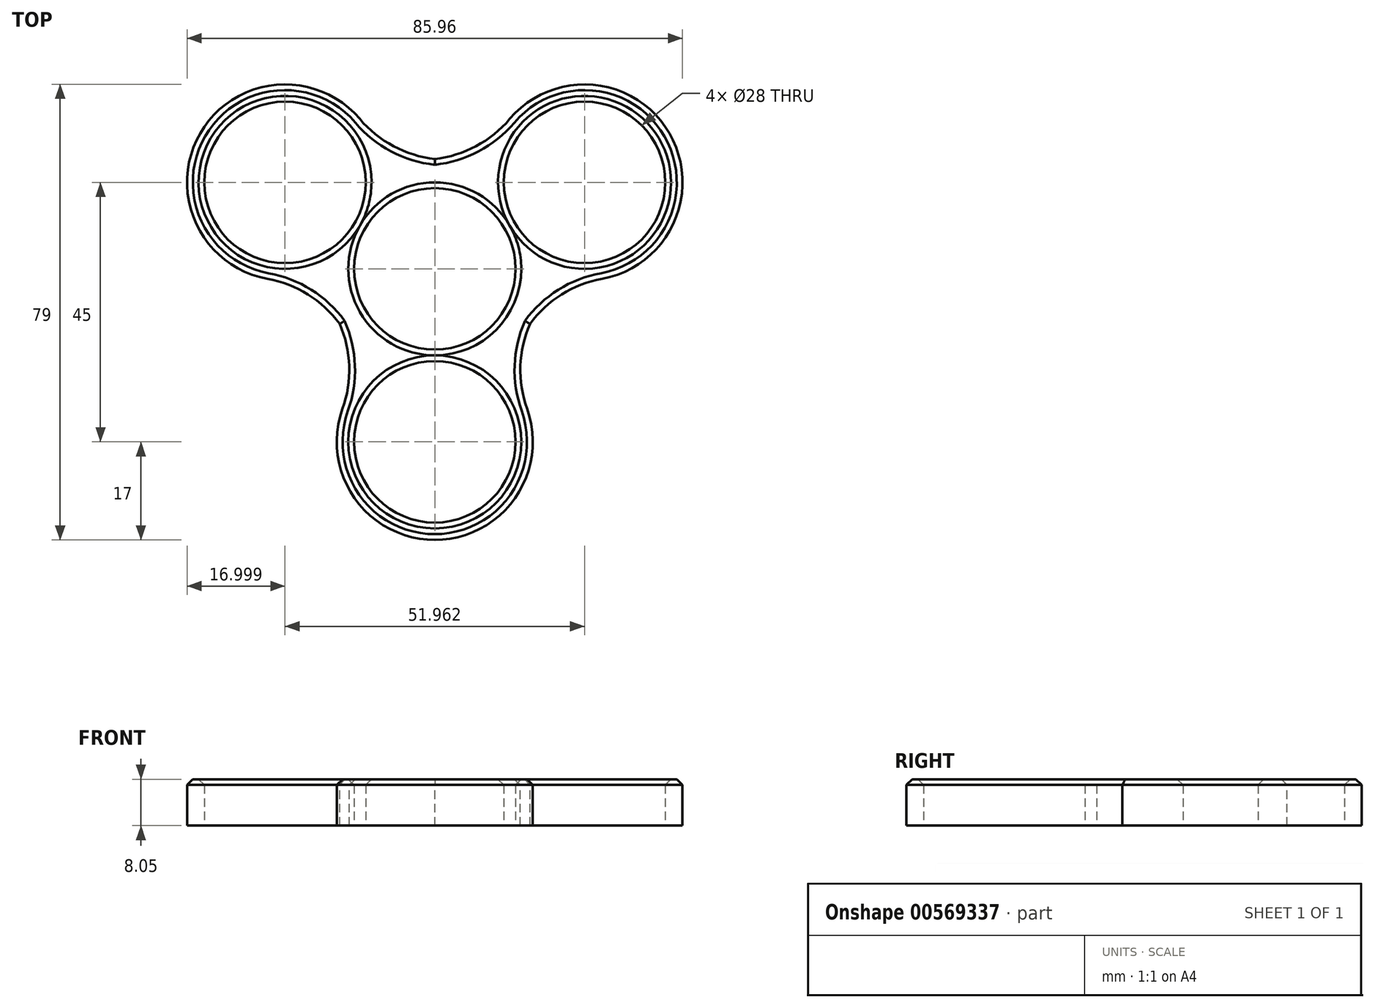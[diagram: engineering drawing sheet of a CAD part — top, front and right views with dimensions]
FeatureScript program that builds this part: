
annotation { "Feature Type Name" : "Feature", "Feature Type Description" : "" }
export const myFeature = defineFeature(function(context is Context, id is Id, definition is map)
    precondition{}
    {
        {
            var Q0;
            Q0=qCreatedBy(makeId("Top.planeOp"),FACE);
            var sketch = newSketch(context, id + "F0", { "sketchPlane" : qUnion([Q0])});
            skCircle(sketch, "E0", {"center": v(0, 0) * mm, "radius": 5.9 * mm});
            skCircle(sketch, "E1", {"center": v(0, 0) * mm, "radius": 14 * mm});
            skArc(sketch, "E2", {"start": v(5.9, -18.06) * mm, "mid": v(6.34, -17.91) * mm, "end": v(6.78, -17.75) * mm});
            skLineSegment(sketch, "E3", {"start": v(5.9, -18.06) * mm, "end": v(5.9, -17.3) * mm});
            skLineSegment(sketch, "E4.trimOffspring", {"start": v(-5.9, -17.3) * mm, "end": v(-5.9, -18.06) * mm});
            skPoint(sketch, "E5.start.orphan", {"position": v(-5.9, 0) * mm});
            skPoint(sketch, "E6.trimOffspring.end.orphan", {"position": v(5.9, 0) * mm});
            skCircle(sketch, "E7", {"center": v(0, -30) * mm, "radius": 14 * mm});
            skArc(sketch, "E8", {"start": v(-9.93, -16.2) * mm, "mid": v(0, -47) * mm, "end": v(9.93, -16.2) * mm});
            skPoint(sketch, "E9.orphan", {"position": v(-5.9, -30) * mm});
            skPoint(sketch, "E10.orphan", {"position": v(5.9, -30) * mm});
            skCircle(sketch, "E11", {"center": v(0, -30) * mm, "radius": 5.9 * mm});
            skCircle(sketch, "E12.1.0", {"center": v(25.98, 15) * mm, "radius": 14 * mm});
            skLineSegment(sketch, "E12.1.1", {"start": v(17.94, 3.54) * mm, "end": v(18.6, 3.92) * mm});
            skArc(sketch, "E12.1.2", {"start": v(19, -0.5) * mm, "mid": v(40.7, 23.5) * mm, "end": v(9.07, 16.7) * mm});
            skPoint(sketch, "E12.1.3", {"position": v(23.03, 20.1) * mm});
            skCircle(sketch, "E12.1.4", {"center": v(25.98, 15) * mm, "radius": 5.9 * mm});
            skLineSegment(sketch, "E12.1.5", {"start": v(12.7, 14.14) * mm, "end": v(12.04, 13.76) * mm});
            skPoint(sketch, "E12.1.6", {"position": v(28.93, 9.9) * mm});
            skCircle(sketch, "E12.2.0", {"center": v(-25.98, 15) * mm, "radius": 14 * mm});
            skLineSegment(sketch, "E12.2.1", {"start": v(-12.04, 13.76) * mm, "end": v(-12.7, 14.14) * mm});
            skArc(sketch, "E12.2.2", {"start": v(-9.07, 16.7) * mm, "mid": v(-40.7, 23.5) * mm, "end": v(-19, -0.5) * mm});
            skPoint(sketch, "E12.2.3", {"position": v(-28.93, 9.9) * mm});
            skCircle(sketch, "E12.2.4", {"center": v(-25.98, 15) * mm, "radius": 5.9 * mm});
            skLineSegment(sketch, "E12.2.5", {"start": v(-18.6, 3.92) * mm, "end": v(-17.94, 3.54) * mm});
            skPoint(sketch, "E12.2.6", {"position": v(-23.03, 20.1) * mm});
            skArc(sketch, "E13.trimOffspring", {"start": v(12.7, 14.14) * mm, "mid": v(12.34, 14.45) * mm, "end": v(11.98, 14.74) * mm});
            skPoint(sketch, "E14.orphan", {"position": v(-5.9, -14.06) * mm});
            skPoint(sketch, "E15.orphan", {"position": v(5.9, -14.06) * mm});
            skArc(sketch, "E16.trimOffspring", {"start": v(9.93, -16.2) * mm, "mid": v(16.45, -9.5) * mm, "end": v(19, -0.5) * mm});
            skPoint(sketch, "E17.orphan", {"position": v(15.12, 1.92) * mm});
            skPoint(sketch, "E18.orphan", {"position": v(-15.12, 1.92) * mm});
            skArc(sketch, "E19.trimOffspring", {"start": v(-19, -0.5) * mm, "mid": v(-16.45, -9.5) * mm, "end": v(-9.93, -16.2) * mm});
            skPoint(sketch, "E20.orphan", {"position": v(-9.22, 12.14) * mm});
            skPoint(sketch, "E21.orphan", {"position": v(9.22, 12.14) * mm});
            skArc(sketch, "E22.trimOffspring", {"start": v(9.07, 16.7) * mm, "mid": v(0, 19) * mm, "end": v(-9.07, 16.7) * mm});
            skSolve(sketch);
        }
        {
            var Q0;
            Q0=makeQuery(id+"F0.imprint","IMPRINT",FACE,{"disambiguationData":[TD([[makeQuery(id+"F0.imprint","IMPRINT",EDGE,{"derivedFrom":sQuery(id+"F0.wireOp",EDGE,"E1")}),-1.0]])]});
            extrude(context, id + "F1", {"entities" : qUnion([Q0]), "depth" : 8.05 * mm, "offsetDistance" : 25 * mm});
        }
        {
            var Q0;
            Q0=makeQuery(id+"F1.opExtrude","SWEPT_EDGE",EDGE,{"disambiguationData":[OSD([sQuery(id+"F0.wireOp",EDGE,"E2"),sQuery(id+"F0.wireOp",EDGE,"E3")])]});
            var Q1;
            Q1=makeQuery(id+"F1.opExtrude","SWEPT_EDGE",EDGE,{"disambiguationData":[OSD([sQuery(id+"F0.wireOp",EDGE,"E2"),sQuery(id+"F0.wireOp",EDGE,"E12.1.1")])]});
            var Q2;
            Q2=makeQuery(id+"F1.opExtrude","SWEPT_EDGE",EDGE,{"disambiguationData":[OSD([sQuery(id+"F0.wireOp",EDGE,"E12.1.1"),sQuery(id+"F0.wireOp",EDGE,"E12.1.2")])]});
            var Q3;
            Q3=makeQuery(id+"F1.opExtrude","SWEPT_EDGE",EDGE,{"disambiguationData":[OSD([sQuery(id+"F0.wireOp",EDGE,"E3"),sQuery(id+"F0.wireOp",EDGE,"E8")])]});
            var Q4;
            Q4=makeQuery(id+"F1.opExtrude","SWEPT_EDGE",EDGE,{"disambiguationData":[OSD([sQuery(id+"F0.wireOp",EDGE,"E12.1.5"),sQuery(id+"F0.wireOp",EDGE,"E13.trimOffspring")])]});
            var Q5;
            Q5=makeQuery(id+"F1.opExtrude","SWEPT_EDGE",EDGE,{"disambiguationData":[OSD([sQuery(id+"F0.wireOp",EDGE,"E12.1.2"),sQuery(id+"F0.wireOp",EDGE,"E12.1.5")])]});
            var Q6;
            Q6=makeQuery(id+"F1.opExtrude","SWEPT_EDGE",EDGE,{"disambiguationData":[OSD([sQuery(id+"F0.wireOp",EDGE,"E12.2.1"),sQuery(id+"F0.wireOp",EDGE,"E13.trimOffspring")])]});
            var Q7;
            Q7=makeQuery(id+"F1.opExtrude","SWEPT_EDGE",EDGE,{"disambiguationData":[OSD([sQuery(id+"F0.wireOp",EDGE,"E12.2.1"),sQuery(id+"F0.wireOp",EDGE,"E12.2.2")])]});
            var Q8;
            Q8=makeQuery(id+"F1.opExtrude","SWEPT_EDGE",EDGE,{"disambiguationData":[OSD([sQuery(id+"F0.wireOp",EDGE,"E12.2.2"),sQuery(id+"F0.wireOp",EDGE,"E12.2.5")])]});
            var Q9;
            Q9=makeQuery(id+"F1.opExtrude","SWEPT_EDGE",EDGE,{"disambiguationData":[OSD([sQuery(id+"F0.wireOp",EDGE,"E12.2.5"),sQuery(id+"F0.wireOp",EDGE,"8e5aad18-0d01-48dc-a158-99cd83f52108.trimOffspring")])]});
            var Q10;
            Q10=makeQuery(id+"F1.opExtrude","SWEPT_EDGE",EDGE,{"disambiguationData":[OSD([sQuery(id+"F0.wireOp",EDGE,"E4.trimOffspring"),sQuery(id+"F0.wireOp",EDGE,"8e5aad18-0d01-48dc-a158-99cd83f52108.trimOffspring")])]});
            var Q11;
            Q11=makeQuery(id+"F1.opExtrude","SWEPT_EDGE",EDGE,{"disambiguationData":[OSD([sQuery(id+"F0.wireOp",EDGE,"E4.trimOffspring"),sQuery(id+"F0.wireOp",EDGE,"E8")])]});
            fillet(context, id + "F2", {"entities" : qUnion([Q0, Q1, Q2, Q3, Q4, Q5, Q6, Q7, Q8, Q9, Q10, Q11]), "radius" : 20 * mm, "tangentPropagation" : true, "allowEdgeOverflow" : false});
        }
        {
            var Q0;
            Q0=makeQuery(id+"F1.opExtrude","CAP_FACE",FACE,{"disambiguationData":[OSD([sQuery(id+"F0.wireOp",EDGE,"E1"),sQuery(id+"F0.wireOp",EDGE,"E7"),sQuery(id+"F0.wireOp",EDGE,"E8"),sQuery(id+"F0.wireOp",EDGE,"E12.1.0"),sQuery(id+"F0.wireOp",EDGE,"E12.1.2"),sQuery(id+"F0.wireOp",EDGE,"E12.2.0"),sQuery(id+"F0.wireOp",EDGE,"E12.2.2"),sQuery(id+"F0.wireOp",EDGE,"E16.trimOffspring"),sQuery(id+"F0.wireOp",EDGE,"E19.trimOffspring"),sQuery(id+"F0.wireOp",EDGE,"E22.trimOffspring")])],"isStart":false});
            chamfer(context, id + "F3", {"entities" : qUnion([Q0]), "width" : 1 * mm, "tangentPropagation" : true});
        }
    });
